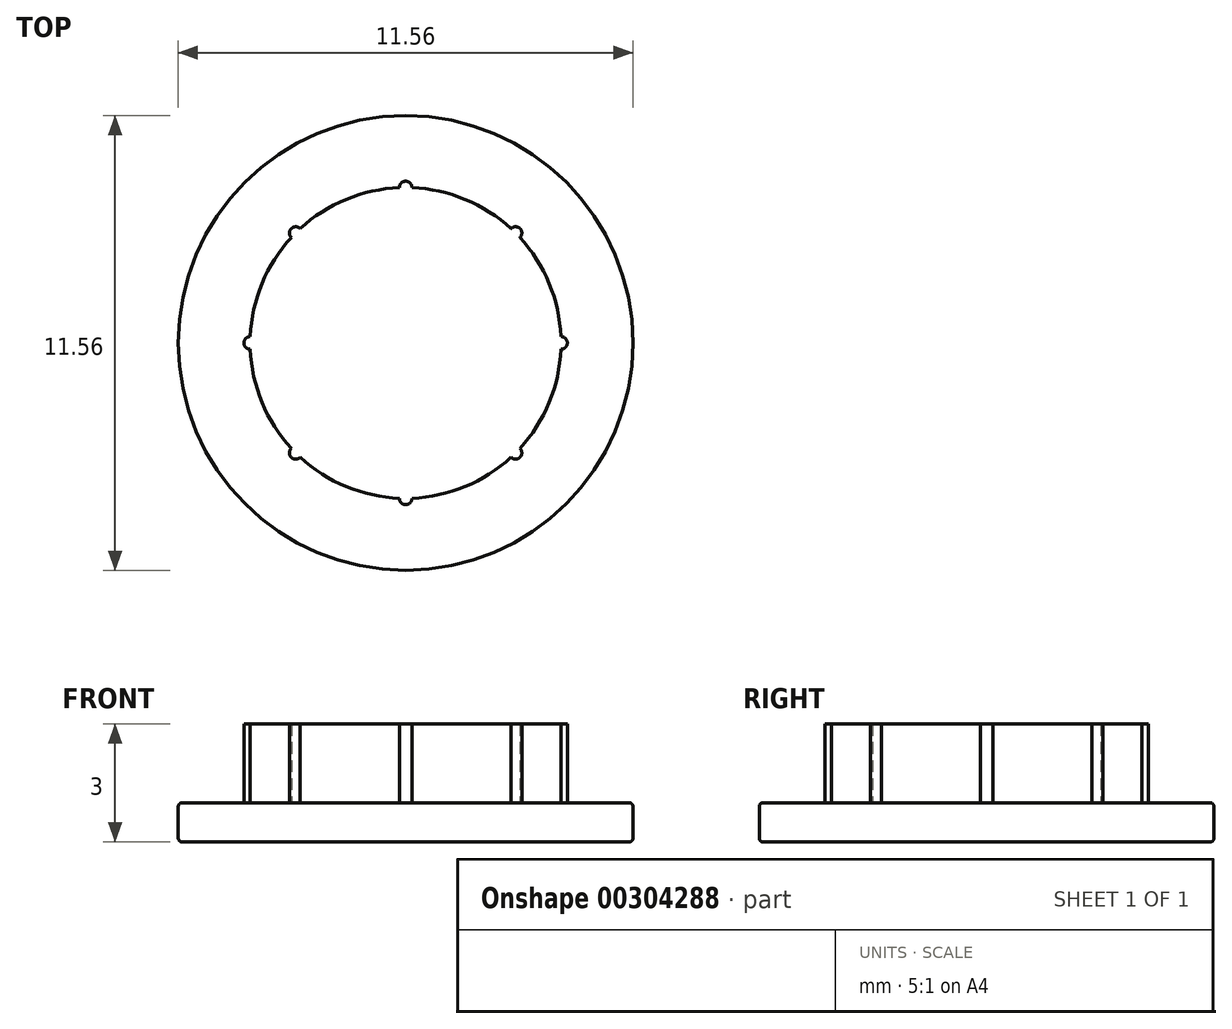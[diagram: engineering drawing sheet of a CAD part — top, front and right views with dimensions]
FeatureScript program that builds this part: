
annotation { "Feature Type Name" : "Feature", "Feature Type Description" : "" }
export const myFeature = defineFeature(function(context is Context, id is Id, definition is map)
    precondition{}
    {
        {
            var Q0;
            Q0=qCreatedBy(makeId("Top.planeOp"),FACE);
            var sketch = newSketch(context, id + "F0", { "sketchPlane" : qUnion([Q0])});
            skCircle(sketch, "E0", {"center": v(0, 0) * mm, "radius": 3.95 * mm});
            skCircle(sketch, "E1", {"center": v(0, 0) * mm, "radius": 5.78 * mm});
            skLineSegment(sketch, "E2", {"start": v(0, 0) * mm, "end": v(3.95, 0) * mm, "construction": true});
            skLineSegment(sketch, "E3", {"start": v(0, 0) * mm, "end": v(0, 3.95) * mm, "construction": true});
            skLineSegment(sketch, "E4", {"start": v(0, 0) * mm, "end": v(-3.95, 0) * mm, "construction": true});
            skLineSegment(sketch, "E5", {"start": v(0, 0) * mm, "end": v(0, -3.95) * mm, "construction": true});
            skCircle(sketch, "E6", {"center": v(0, -3.95) * mm, "radius": 0.16 * mm});
            skCircle(sketch, "E7.1.0", {"center": v(-2.8, -2.8) * mm, "radius": 0.16 * mm});
            skCircle(sketch, "E7.2.0", {"center": v(-3.95, 0) * mm, "radius": 0.16 * mm});
            skCircle(sketch, "E8.1.0", {"center": v(-2.8, 2.8) * mm, "radius": 0.16 * mm});
            skCircle(sketch, "E8.2.0", {"center": v(0, 3.95) * mm, "radius": 0.16 * mm});
            skCircle(sketch, "E9.1.0", {"center": v(2.8, 2.8) * mm, "radius": 0.16 * mm});
            skCircle(sketch, "E9.2.0", {"center": v(3.95, 0) * mm, "radius": 0.16 * mm});
            skCircle(sketch, "E10.1.0", {"center": v(2.8, -2.8) * mm, "radius": 0.16 * mm});
            skSolve(sketch);
        }
        {
            var Q0;
            {var subQ0=sQuery(id+"F0.wireOp",EDGE,"E7.2.0");var subQ1=sQuery(id+"F0.wireOp",EDGE,"E0");var subQ2=makeQuery(id+"F0.imprint","INTERSECT",VERTEX,{"disambiguationData":[OD(0.0)],"derivedFrom":[subQ1,subQ0]});Q0=makeQuery(id+"F0.imprint","IMPRINT",FACE,{"disambiguationData":[TD([[makeQuery(id+"F0.imprint","IMPRINT",EDGE,{"disambiguationData":[TD([[subQ2,-1.0]])],"derivedFrom":subQ1}),-1.0]])]});}
            var Q1;
            {var subQ0=sQuery(id+"F0.wireOp",EDGE,"E7.2.0");var subQ1=sQuery(id+"F0.wireOp",EDGE,"E0");var subQ2=makeQuery(id+"F0.imprint","INTERSECT",VERTEX,{"disambiguationData":[OD(0.0)],"derivedFrom":[subQ1,subQ0]});Q1=makeQuery(id+"F0.imprint","IMPRINT",FACE,{"disambiguationData":[TD([[makeQuery(id+"F0.imprint","IMPRINT",EDGE,{"disambiguationData":[TD([[subQ2,-1.0]])],"derivedFrom":subQ1}),1.0]])]});}
            var Q2;
            Q2=makeQuery(id+"F0.imprint","IMPRINT",FACE,{"disambiguationData":[TD([[makeQuery(id+"F0.imprint","IMPRINT",EDGE,{"derivedFrom":sQuery(id+"F0.wireOp",EDGE,"E1")}),1.0]])]});
            var Q3;
            {var subQ1=sQuery(id+"F0.wireOp",EDGE,"E0");var subQ15=sQuery(id+"F0.wireOp",EDGE,"E9.1.0");var subQ16=makeQuery(id+"F0.imprint","INTERSECT",VERTEX,{"disambiguationData":[OD(0.0)],"derivedFrom":[subQ1,subQ15]});Q3=makeQuery(id+"F0.imprint","IMPRINT",FACE,{"disambiguationData":[TD([[makeQuery(id+"F0.imprint","IMPRINT",EDGE,{"disambiguationData":[TD([[subQ16,1.0]])],"derivedFrom":subQ1}),1.0]])]});}
            var Q4;
            {var subQ0=sQuery(id+"F0.wireOp",EDGE,"E7.1.0");var subQ1=sQuery(id+"F0.wireOp",EDGE,"E0");var subQ2=makeQuery(id+"F0.imprint","INTERSECT",VERTEX,{"disambiguationData":[OD(0.0)],"derivedFrom":[subQ1,subQ0]});Q4=makeQuery(id+"F0.imprint","IMPRINT",FACE,{"disambiguationData":[TD([[makeQuery(id+"F0.imprint","IMPRINT",EDGE,{"disambiguationData":[TD([[subQ2,-1.0]])],"derivedFrom":subQ1}),-1.0]])]});}
            var Q5;
            {var subQ0=sQuery(id+"F0.wireOp",EDGE,"E7.1.0");var subQ1=sQuery(id+"F0.wireOp",EDGE,"E0");var subQ2=makeQuery(id+"F0.imprint","INTERSECT",VERTEX,{"disambiguationData":[OD(0.0)],"derivedFrom":[subQ1,subQ0]});Q5=makeQuery(id+"F0.imprint","IMPRINT",FACE,{"disambiguationData":[TD([[makeQuery(id+"F0.imprint","IMPRINT",EDGE,{"disambiguationData":[TD([[subQ2,-1.0]])],"derivedFrom":subQ1}),1.0]])]});}
            var Q6;
            {var subQ0=sQuery(id+"F0.wireOp",EDGE,"E8.1.0");var subQ1=sQuery(id+"F0.wireOp",EDGE,"E0");var subQ2=makeQuery(id+"F0.imprint","INTERSECT",VERTEX,{"disambiguationData":[OD(0.0)],"derivedFrom":[subQ1,subQ0]});Q6=makeQuery(id+"F0.imprint","IMPRINT",FACE,{"disambiguationData":[TD([[makeQuery(id+"F0.imprint","IMPRINT",EDGE,{"disambiguationData":[TD([[subQ2,-1.0]])],"derivedFrom":subQ1}),-1.0]])]});}
            var Q7;
            {var subQ0=sQuery(id+"F0.wireOp",EDGE,"E8.1.0");var subQ1=sQuery(id+"F0.wireOp",EDGE,"E0");var subQ2=makeQuery(id+"F0.imprint","INTERSECT",VERTEX,{"disambiguationData":[OD(0.0)],"derivedFrom":[subQ1,subQ0]});Q7=makeQuery(id+"F0.imprint","IMPRINT",FACE,{"disambiguationData":[TD([[makeQuery(id+"F0.imprint","IMPRINT",EDGE,{"disambiguationData":[TD([[subQ2,-1.0]])],"derivedFrom":subQ1}),1.0]])]});}
            var Q8;
            {var subQ0=sQuery(id+"F0.wireOp",EDGE,"E9.2.0");var subQ1=sQuery(id+"F0.wireOp",EDGE,"E0");var subQ2=makeQuery(id+"F0.imprint","INTERSECT",VERTEX,{"disambiguationData":[OD(0.0)],"derivedFrom":[subQ1,subQ0]});Q8=makeQuery(id+"F0.imprint","IMPRINT",FACE,{"disambiguationData":[TD([[makeQuery(id+"F0.imprint","IMPRINT",EDGE,{"disambiguationData":[TD([[subQ2,1.0]])],"derivedFrom":subQ1}),-1.0]])]});}
            var Q9;
            {var subQ0=sQuery(id+"F0.wireOp",EDGE,"E9.2.0");var subQ1=sQuery(id+"F0.wireOp",EDGE,"E0");var subQ2=makeQuery(id+"F0.imprint","INTERSECT",VERTEX,{"disambiguationData":[OD(0.0)],"derivedFrom":[subQ1,subQ0]});Q9=makeQuery(id+"F0.imprint","IMPRINT",FACE,{"disambiguationData":[TD([[makeQuery(id+"F0.imprint","IMPRINT",EDGE,{"disambiguationData":[TD([[subQ2,1.0]])],"derivedFrom":subQ1}),1.0]])]});}
            var Q10;
            {var subQ0=sQuery(id+"F0.wireOp",EDGE,"E10.1.0");var subQ1=sQuery(id+"F0.wireOp",EDGE,"E0");var subQ2=makeQuery(id+"F0.imprint","INTERSECT",VERTEX,{"disambiguationData":[OD(0.0)],"derivedFrom":[subQ1,subQ0]});Q10=makeQuery(id+"F0.imprint","IMPRINT",FACE,{"disambiguationData":[TD([[makeQuery(id+"F0.imprint","IMPRINT",EDGE,{"disambiguationData":[TD([[subQ2,-1.0]])],"derivedFrom":subQ1}),1.0]])]});}
            var Q11;
            {var subQ0=sQuery(id+"F0.wireOp",EDGE,"E10.1.0");var subQ1=sQuery(id+"F0.wireOp",EDGE,"E0");var subQ2=makeQuery(id+"F0.imprint","INTERSECT",VERTEX,{"disambiguationData":[OD(0.0)],"derivedFrom":[subQ1,subQ0]});Q11=makeQuery(id+"F0.imprint","IMPRINT",FACE,{"disambiguationData":[TD([[makeQuery(id+"F0.imprint","IMPRINT",EDGE,{"disambiguationData":[TD([[subQ2,-1.0]])],"derivedFrom":subQ1}),-1.0]])]});}
            var Q12;
            {var subQ0=sQuery(id+"F0.wireOp",EDGE,"E6");var subQ1=sQuery(id+"F0.wireOp",EDGE,"E0");var subQ2=makeQuery(id+"F0.imprint","INTERSECT",VERTEX,{"disambiguationData":[OD(0.0)],"derivedFrom":[subQ1,subQ0]});Q12=makeQuery(id+"F0.imprint","IMPRINT",FACE,{"disambiguationData":[TD([[makeQuery(id+"F0.imprint","IMPRINT",EDGE,{"disambiguationData":[TD([[subQ2,-1.0]])],"derivedFrom":subQ1}),-1.0]])]});}
            var Q13;
            {var subQ0=sQuery(id+"F0.wireOp",EDGE,"E6");var subQ1=sQuery(id+"F0.wireOp",EDGE,"E0");var subQ2=makeQuery(id+"F0.imprint","INTERSECT",VERTEX,{"disambiguationData":[OD(0.0)],"derivedFrom":[subQ1,subQ0]});Q13=makeQuery(id+"F0.imprint","IMPRINT",FACE,{"disambiguationData":[TD([[makeQuery(id+"F0.imprint","IMPRINT",EDGE,{"disambiguationData":[TD([[subQ2,-1.0]])],"derivedFrom":subQ1}),1.0]])]});}
            var Q14;
            {var subQ0=sQuery(id+"F0.wireOp",EDGE,"E9.1.0");var subQ1=sQuery(id+"F0.wireOp",EDGE,"E0");var subQ2=makeQuery(id+"F0.imprint","INTERSECT",VERTEX,{"disambiguationData":[OD(0.0)],"derivedFrom":[subQ1,subQ0]});Q14=makeQuery(id+"F0.imprint","IMPRINT",FACE,{"disambiguationData":[TD([[makeQuery(id+"F0.imprint","IMPRINT",EDGE,{"disambiguationData":[TD([[subQ2,-1.0]])],"derivedFrom":subQ1}),-1.0]])]});}
            var Q15;
            {var subQ0=sQuery(id+"F0.wireOp",EDGE,"E9.1.0");var subQ1=sQuery(id+"F0.wireOp",EDGE,"E0");var subQ2=makeQuery(id+"F0.imprint","INTERSECT",VERTEX,{"disambiguationData":[OD(0.0)],"derivedFrom":[subQ1,subQ0]});Q15=makeQuery(id+"F0.imprint","IMPRINT",FACE,{"disambiguationData":[TD([[makeQuery(id+"F0.imprint","IMPRINT",EDGE,{"disambiguationData":[TD([[subQ2,-1.0]])],"derivedFrom":subQ1}),1.0]])]});}
            var Q16;
            {var subQ0=sQuery(id+"F0.wireOp",EDGE,"E8.2.0");var subQ1=sQuery(id+"F0.wireOp",EDGE,"E0");var subQ2=makeQuery(id+"F0.imprint","INTERSECT",VERTEX,{"disambiguationData":[OD(0.0)],"derivedFrom":[subQ1,subQ0]});Q16=makeQuery(id+"F0.imprint","IMPRINT",FACE,{"disambiguationData":[TD([[makeQuery(id+"F0.imprint","IMPRINT",EDGE,{"disambiguationData":[TD([[subQ2,-1.0]])],"derivedFrom":subQ1}),1.0]])]});}
            var Q17;
            {var subQ0=sQuery(id+"F0.wireOp",EDGE,"E8.2.0");var subQ1=sQuery(id+"F0.wireOp",EDGE,"E0");var subQ2=makeQuery(id+"F0.imprint","INTERSECT",VERTEX,{"disambiguationData":[OD(0.0)],"derivedFrom":[subQ1,subQ0]});Q17=makeQuery(id+"F0.imprint","IMPRINT",FACE,{"disambiguationData":[TD([[makeQuery(id+"F0.imprint","IMPRINT",EDGE,{"disambiguationData":[TD([[subQ2,-1.0]])],"derivedFrom":subQ1}),-1.0]])]});}
            extrude(context, id + "F1", {"entities" : qUnion([Q0, Q1, Q2, Q3, Q4, Q5, Q6, Q7, Q8, Q9, Q10, Q11, Q12, Q13, Q14, Q15, Q16, Q17]), "oppositeDirection" : true, "depth" : 1 * mm});
        }
        {
            var Q0;
            {var subQ1=sQuery(id+"F0.wireOp",EDGE,"E0");var subQ15=sQuery(id+"F0.wireOp",EDGE,"E9.1.0");var subQ16=makeQuery(id+"F0.imprint","INTERSECT",VERTEX,{"disambiguationData":[OD(0.0)],"derivedFrom":[subQ1,subQ15]});Q0=makeQuery(id+"F0.imprint","IMPRINT",FACE,{"disambiguationData":[TD([[makeQuery(id+"F0.imprint","IMPRINT",EDGE,{"disambiguationData":[TD([[subQ16,1.0]])],"derivedFrom":subQ1}),1.0]])]});}
            var Q1;
            {var subQ0=sQuery(id+"F0.wireOp",EDGE,"E8.1.0");var subQ1=sQuery(id+"F0.wireOp",EDGE,"E0");var subQ2=makeQuery(id+"F0.imprint","INTERSECT",VERTEX,{"disambiguationData":[OD(0.0)],"derivedFrom":[subQ1,subQ0]});Q1=makeQuery(id+"F0.imprint","IMPRINT",FACE,{"disambiguationData":[TD([[makeQuery(id+"F0.imprint","IMPRINT",EDGE,{"disambiguationData":[TD([[subQ2,-1.0]])],"derivedFrom":subQ1}),1.0]])]});}
            var Q2;
            {var subQ0=sQuery(id+"F0.wireOp",EDGE,"E8.1.0");var subQ1=sQuery(id+"F0.wireOp",EDGE,"E0");var subQ2=makeQuery(id+"F0.imprint","INTERSECT",VERTEX,{"disambiguationData":[OD(0.0)],"derivedFrom":[subQ1,subQ0]});Q2=makeQuery(id+"F0.imprint","IMPRINT",FACE,{"disambiguationData":[TD([[makeQuery(id+"F0.imprint","IMPRINT",EDGE,{"disambiguationData":[TD([[subQ2,-1.0]])],"derivedFrom":subQ1}),-1.0]])]});}
            var Q3;
            {var subQ0=sQuery(id+"F0.wireOp",EDGE,"E7.2.0");var subQ1=sQuery(id+"F0.wireOp",EDGE,"E0");var subQ2=makeQuery(id+"F0.imprint","INTERSECT",VERTEX,{"disambiguationData":[OD(0.0)],"derivedFrom":[subQ1,subQ0]});Q3=makeQuery(id+"F0.imprint","IMPRINT",FACE,{"disambiguationData":[TD([[makeQuery(id+"F0.imprint","IMPRINT",EDGE,{"disambiguationData":[TD([[subQ2,-1.0]])],"derivedFrom":subQ1}),-1.0]])]});}
            var Q4;
            {var subQ0=sQuery(id+"F0.wireOp",EDGE,"E7.2.0");var subQ1=sQuery(id+"F0.wireOp",EDGE,"E0");var subQ2=makeQuery(id+"F0.imprint","INTERSECT",VERTEX,{"disambiguationData":[OD(0.0)],"derivedFrom":[subQ1,subQ0]});Q4=makeQuery(id+"F0.imprint","IMPRINT",FACE,{"disambiguationData":[TD([[makeQuery(id+"F0.imprint","IMPRINT",EDGE,{"disambiguationData":[TD([[subQ2,-1.0]])],"derivedFrom":subQ1}),1.0]])]});}
            var Q5;
            {var subQ0=sQuery(id+"F0.wireOp",EDGE,"E7.1.0");var subQ1=sQuery(id+"F0.wireOp",EDGE,"E0");var subQ2=makeQuery(id+"F0.imprint","INTERSECT",VERTEX,{"disambiguationData":[OD(0.0)],"derivedFrom":[subQ1,subQ0]});Q5=makeQuery(id+"F0.imprint","IMPRINT",FACE,{"disambiguationData":[TD([[makeQuery(id+"F0.imprint","IMPRINT",EDGE,{"disambiguationData":[TD([[subQ2,-1.0]])],"derivedFrom":subQ1}),-1.0]])]});}
            var Q6;
            {var subQ0=sQuery(id+"F0.wireOp",EDGE,"E7.1.0");var subQ1=sQuery(id+"F0.wireOp",EDGE,"E0");var subQ2=makeQuery(id+"F0.imprint","INTERSECT",VERTEX,{"disambiguationData":[OD(0.0)],"derivedFrom":[subQ1,subQ0]});Q6=makeQuery(id+"F0.imprint","IMPRINT",FACE,{"disambiguationData":[TD([[makeQuery(id+"F0.imprint","IMPRINT",EDGE,{"disambiguationData":[TD([[subQ2,-1.0]])],"derivedFrom":subQ1}),1.0]])]});}
            var Q7;
            {var subQ0=sQuery(id+"F0.wireOp",EDGE,"E6");var subQ1=sQuery(id+"F0.wireOp",EDGE,"E0");var subQ2=makeQuery(id+"F0.imprint","INTERSECT",VERTEX,{"disambiguationData":[OD(0.0)],"derivedFrom":[subQ1,subQ0]});Q7=makeQuery(id+"F0.imprint","IMPRINT",FACE,{"disambiguationData":[TD([[makeQuery(id+"F0.imprint","IMPRINT",EDGE,{"disambiguationData":[TD([[subQ2,-1.0]])],"derivedFrom":subQ1}),-1.0]])]});}
            var Q8;
            {var subQ0=sQuery(id+"F0.wireOp",EDGE,"E6");var subQ1=sQuery(id+"F0.wireOp",EDGE,"E0");var subQ2=makeQuery(id+"F0.imprint","INTERSECT",VERTEX,{"disambiguationData":[OD(0.0)],"derivedFrom":[subQ1,subQ0]});Q8=makeQuery(id+"F0.imprint","IMPRINT",FACE,{"disambiguationData":[TD([[makeQuery(id+"F0.imprint","IMPRINT",EDGE,{"disambiguationData":[TD([[subQ2,-1.0]])],"derivedFrom":subQ1}),1.0]])]});}
            var Q9;
            {var subQ0=sQuery(id+"F0.wireOp",EDGE,"E10.1.0");var subQ1=sQuery(id+"F0.wireOp",EDGE,"E0");var subQ2=makeQuery(id+"F0.imprint","INTERSECT",VERTEX,{"disambiguationData":[OD(0.0)],"derivedFrom":[subQ1,subQ0]});Q9=makeQuery(id+"F0.imprint","IMPRINT",FACE,{"disambiguationData":[TD([[makeQuery(id+"F0.imprint","IMPRINT",EDGE,{"disambiguationData":[TD([[subQ2,-1.0]])],"derivedFrom":subQ1}),-1.0]])]});}
            var Q10;
            {var subQ0=sQuery(id+"F0.wireOp",EDGE,"E10.1.0");var subQ1=sQuery(id+"F0.wireOp",EDGE,"E0");var subQ2=makeQuery(id+"F0.imprint","INTERSECT",VERTEX,{"disambiguationData":[OD(0.0)],"derivedFrom":[subQ1,subQ0]});Q10=makeQuery(id+"F0.imprint","IMPRINT",FACE,{"disambiguationData":[TD([[makeQuery(id+"F0.imprint","IMPRINT",EDGE,{"disambiguationData":[TD([[subQ2,-1.0]])],"derivedFrom":subQ1}),1.0]])]});}
            var Q11;
            {var subQ0=sQuery(id+"F0.wireOp",EDGE,"E9.2.0");var subQ1=sQuery(id+"F0.wireOp",EDGE,"E0");var subQ2=makeQuery(id+"F0.imprint","INTERSECT",VERTEX,{"disambiguationData":[OD(0.0)],"derivedFrom":[subQ1,subQ0]});Q11=makeQuery(id+"F0.imprint","IMPRINT",FACE,{"disambiguationData":[TD([[makeQuery(id+"F0.imprint","IMPRINT",EDGE,{"disambiguationData":[TD([[subQ2,1.0]])],"derivedFrom":subQ1}),1.0]])]});}
            var Q12;
            {var subQ0=sQuery(id+"F0.wireOp",EDGE,"E9.2.0");var subQ1=sQuery(id+"F0.wireOp",EDGE,"E0");var subQ2=makeQuery(id+"F0.imprint","INTERSECT",VERTEX,{"disambiguationData":[OD(0.0)],"derivedFrom":[subQ1,subQ0]});Q12=makeQuery(id+"F0.imprint","IMPRINT",FACE,{"disambiguationData":[TD([[makeQuery(id+"F0.imprint","IMPRINT",EDGE,{"disambiguationData":[TD([[subQ2,1.0]])],"derivedFrom":subQ1}),-1.0]])]});}
            var Q13;
            {var subQ0=sQuery(id+"F0.wireOp",EDGE,"E8.2.0");var subQ1=sQuery(id+"F0.wireOp",EDGE,"E0");var subQ2=makeQuery(id+"F0.imprint","INTERSECT",VERTEX,{"disambiguationData":[OD(0.0)],"derivedFrom":[subQ1,subQ0]});Q13=makeQuery(id+"F0.imprint","IMPRINT",FACE,{"disambiguationData":[TD([[makeQuery(id+"F0.imprint","IMPRINT",EDGE,{"disambiguationData":[TD([[subQ2,-1.0]])],"derivedFrom":subQ1}),-1.0]])]});}
            var Q14;
            {var subQ0=sQuery(id+"F0.wireOp",EDGE,"E8.2.0");var subQ1=sQuery(id+"F0.wireOp",EDGE,"E0");var subQ2=makeQuery(id+"F0.imprint","INTERSECT",VERTEX,{"disambiguationData":[OD(0.0)],"derivedFrom":[subQ1,subQ0]});Q14=makeQuery(id+"F0.imprint","IMPRINT",FACE,{"disambiguationData":[TD([[makeQuery(id+"F0.imprint","IMPRINT",EDGE,{"disambiguationData":[TD([[subQ2,-1.0]])],"derivedFrom":subQ1}),1.0]])]});}
            var Q15;
            {var subQ0=sQuery(id+"F0.wireOp",EDGE,"E9.1.0");var subQ1=sQuery(id+"F0.wireOp",EDGE,"E0");var subQ2=makeQuery(id+"F0.imprint","INTERSECT",VERTEX,{"disambiguationData":[OD(0.0)],"derivedFrom":[subQ1,subQ0]});Q15=makeQuery(id+"F0.imprint","IMPRINT",FACE,{"disambiguationData":[TD([[makeQuery(id+"F0.imprint","IMPRINT",EDGE,{"disambiguationData":[TD([[subQ2,-1.0]])],"derivedFrom":subQ1}),1.0]])]});}
            var Q16;
            {var subQ0=sQuery(id+"F0.wireOp",EDGE,"E9.1.0");var subQ1=sQuery(id+"F0.wireOp",EDGE,"E0");var subQ2=makeQuery(id+"F0.imprint","INTERSECT",VERTEX,{"disambiguationData":[OD(0.0)],"derivedFrom":[subQ1,subQ0]});Q16=makeQuery(id+"F0.imprint","IMPRINT",FACE,{"disambiguationData":[TD([[makeQuery(id+"F0.imprint","IMPRINT",EDGE,{"disambiguationData":[TD([[subQ2,-1.0]])],"derivedFrom":subQ1}),-1.0]])]});}
            extrude(context, id + "F2", {"entities" : qUnion([Q0, Q1, Q2, Q3, Q4, Q5, Q6, Q7, Q8, Q9, Q10, Q11, Q12, Q13, Q14, Q15, Q16]), "operationType" : NewBodyOperationType.ADD, "depth" : 2 * mm});
        }
        {
            var Q0;
            Q0=makeQuery(id+"F1.opExtrude","CAP_EDGE",EDGE,{"disambiguationData":[OSD([sQuery(id+"F0.wireOp",EDGE,"E1")])],"isStart":false});
            var Q1;
            Q1=makeQuery(id+"F1.opExtrude","CAP_EDGE",EDGE,{"disambiguationData":[OSD([sQuery(id+"F0.wireOp",EDGE,"E1")])],"isStart":true});
            fillet(context, id + "F3", {"entities" : qUnion([Q0, Q1]), "radius" : 0.1 * mm, "tangentPropagation" : true, "allowEdgeOverflow" : false});
        }
    });
